# Revit family: HD091-2016.02.29-BT- Cielo Tubrise Horizontal
name_source: partatom
category: Modelos genéricos
revit_build: Autodesk Revit 2017 (Build: 20160225_1515(x64)
units: mm (PartAtom-declared; Revit-internal decimal feet)

## family parameters
Compartido = No
Corte con vacíos al cargar = No
Cota de conector redondo = Diámetro de uso
Puede alojar armadura = No
Punto de cálculo de habitación = No
Se basa en plano de trabajo = No
Siempre vertical = Sí
Tipo de pieza = Normal

## types (1)
- Productos HD
    Abrazadera = 13
    BT_Alto = 900 mm
    BT_Ancho = Ø40
    BT_Codigo_Origen = HD091
    BT_Color = 100 colores a eleccion
    BT_Código_Línea = De Linea
    BT_Descripcion = El Cielo Tubrise ha sido diseñado para ser usado como cortasol cenital, entregando a sus proyectos una atractiva terminación.
    BT_EETT = Su geometría es en base a tubos metálicos de un diámetro fijo, los cuales pueden ser instalados de forma paralela. La separación entre ellos es variable, por lo que depende de los requerimientos del proyectista
    BT_Elemento = Cielos
    BT_Especialidad = Arquitectura
    BT_Fabricante = Hunter Douglas
    BT_Itemizado_Estandar_CDT = D 04 04 80
    BT_Marca = Hunter Douglas
    BT_MasterFormat® = 09 54 23
    BT_Material = Aluzinc/Aluminio
    BT_Nombre_Corto = Cielo Tubrise horizontal
    BT_Nombre_Tecnico = Cielo Tubrise horizontal
    BT_Peso = 10.58 kg/m2 / 3.77 kg/m2
    BT_Profundidad = Largo Máximo 6 mts
    BT_SKU = 00 30 21
    BT_Uso = Interior
    BT_Web_del_Producto = http://www.hunterdouglas.cl
    Cant Paneles = 15
    ID_Objeto = BT_F_F_713
    ID_Source = BIMTOOL
    Largo Z = 1400 mm  [stored 4.59318 ft]

note: [stored X ft] marks values corroborated as IEEE doubles in the binary element streams (Revit-internal decimal feet)

## geometry (parser evidence)
native form markers: Sweep x87
no freeform markers — native parametric forms only
